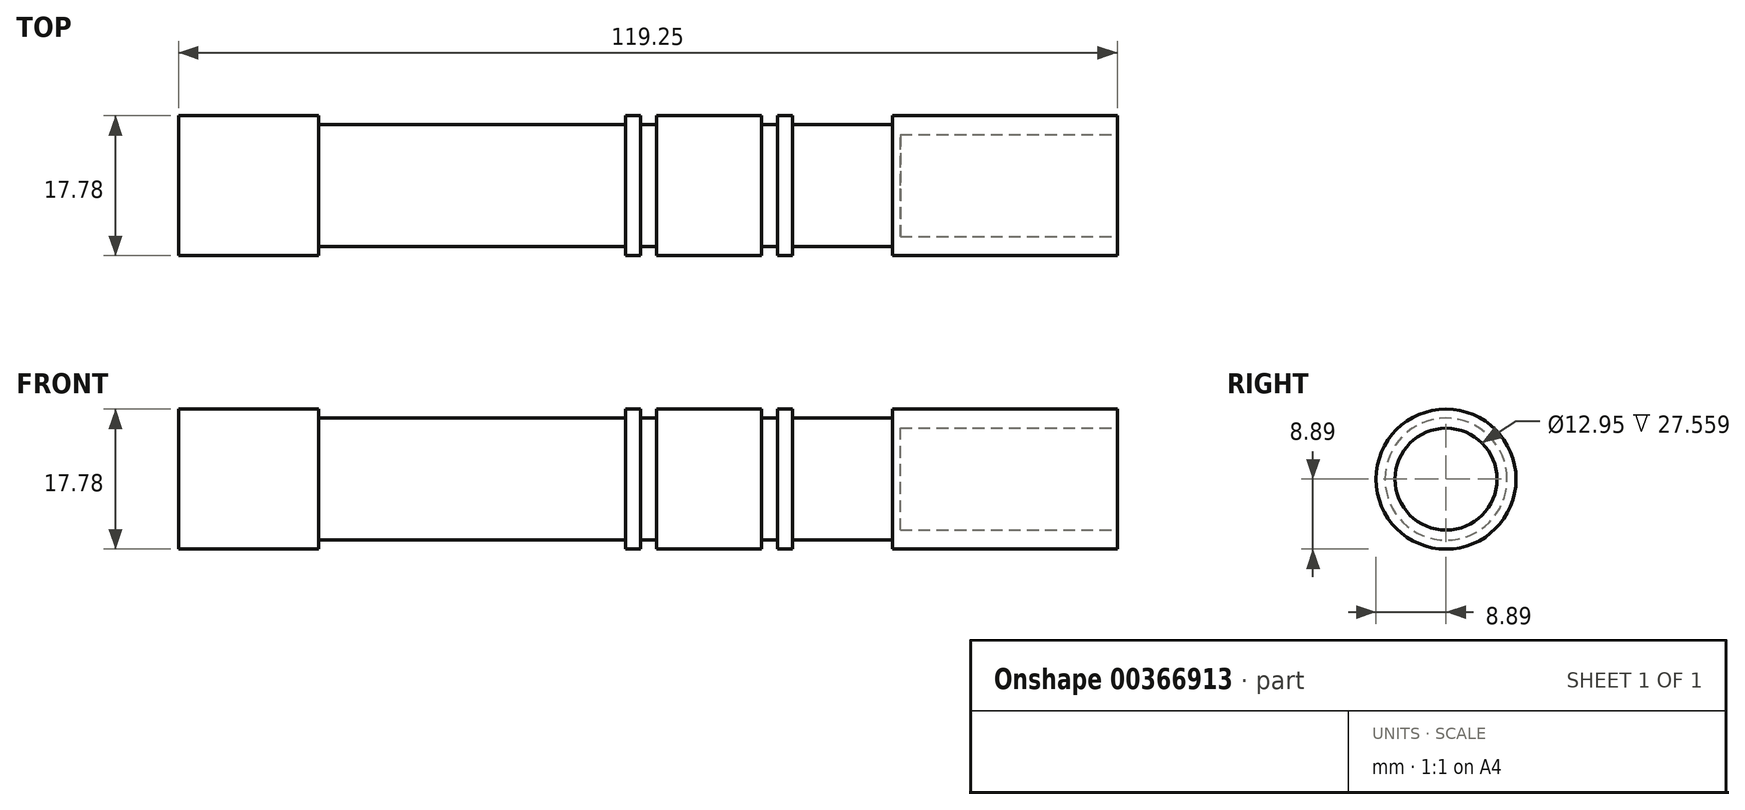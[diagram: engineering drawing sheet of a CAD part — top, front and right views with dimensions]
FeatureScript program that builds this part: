
annotation { "Feature Type Name" : "Feature", "Feature Type Description" : "" }
export const myFeature = defineFeature(function(context is Context, id is Id, definition is map)
    precondition{}
    {
        {
            var Q0;
            Q0=qCreatedBy(makeId("Right.planeOp"),FACE);
            var sketch = newSketch(context, id + "F0", { "sketchPlane" : qUnion([Q0])});
            skCircle(sketch, "E0", {"center": v(0, 0) * mm, "radius": 8.89 * mm});
            skSolve(sketch);
        }
        {
            var Q0;
            Q0 = qSketchRegion(id + "F0", true);
            extrude(context, id + "F1", {"entities" : qUnion([Q0]), "depth" : 17.78 * mm, "offsetDistance" : 25.4 * mm});
        }
        {
            var Q0;
            Q0=makeQuery(id+"F1.opExtrude","CAP_FACE",FACE,{"disambiguationData":[OSD([sQuery(id+"F0.wireOp",EDGE,"E0")])],"isStart":false});
            var sketch = newSketch(context, id + "F2", { "sketchPlane" : qUnion([Q0])});
            skCircle(sketch, "E1", {"center": v(0, 0) * mm, "radius": 7.75 * mm});
            skSolve(sketch);
        }
        {
            var Q0;
            Q0 = qSketchRegion(id + "F2", true);
            extrude(context, id + "F3", {"entities" : qUnion([Q0]), "operationType" : NewBodyOperationType.ADD, "depth" : 39 * mm, "offsetDistance" : 25.4 * mm});
        }
        {
            var Q0;
            Q0=makeQuery(id+"F3.opExtrude","CAP_FACE",FACE,{"disambiguationData":[OSD([sQuery(id+"F2.wireOp",EDGE,"E1")])],"isStart":false});
            var sketch = newSketch(context, id + "F4", { "sketchPlane" : qUnion([Q0])});
            skCircle(sketch, "E2", {"center": v(0, 0) * mm, "radius": 8.9 * mm});
            skSolve(sketch);
        }
        {
            var Q0;
            Q0 = qSketchRegion(id + "F4", true);
            extrude(context, id + "F5", {"entities" : qUnion([Q0]), "operationType" : NewBodyOperationType.ADD, "depth" : 1.9 * mm, "offsetDistance" : 25.4 * mm});
        }
        {
            var Q0;
            Q0=makeQuery(id+"F5.opExtrude","CAP_FACE",FACE,{"disambiguationData":[OSD([sQuery(id+"F4.wireOp",EDGE,"E2")])],"isStart":false});
            var sketch = newSketch(context, id + "F6", { "sketchPlane" : qUnion([Q0])});
            skCircle(sketch, "E3", {"center": v(0, 0) * mm, "radius": 7.75 * mm});
            skSolve(sketch);
        }
        {
            var Q0;
            Q0 = qSketchRegion(id + "F6", true);
            extrude(context, id + "F7", {"entities" : qUnion([Q0]), "operationType" : NewBodyOperationType.ADD, "depth" : 2.03 * mm, "offsetDistance" : 25.4 * mm});
        }
        {
            var Q0;
            Q0=makeQuery(id+"F7.opExtrude","CAP_FACE",FACE,{"disambiguationData":[OSD([sQuery(id+"F6.wireOp",EDGE,"E3")])],"isStart":false});
            var sketch = newSketch(context, id + "F8", { "sketchPlane" : qUnion([Q0])});
            skCircle(sketch, "E4", {"center": v(0, 0) * mm, "radius": 8.9 * mm});
            skSolve(sketch);
        }
        {
            var Q0;
            Q0 = qSketchRegion(id + "F8", true);
            extrude(context, id + "F9", {"entities" : qUnion([Q0]), "operationType" : NewBodyOperationType.ADD, "depth" : 13.33 * mm, "offsetDistance" : 25.4 * mm});
        }
        {
            var Q0;
            Q0=makeQuery(id+"F9.opExtrude","CAP_FACE",FACE,{"disambiguationData":[OSD([sQuery(id+"F8.wireOp",EDGE,"E4")])],"isStart":false});
            var sketch = newSketch(context, id + "F10", { "sketchPlane" : qUnion([Q0])});
            skCircle(sketch, "E5", {"center": v(0, 0) * mm, "radius": 7.75 * mm});
            skSolve(sketch);
        }
        {
            var Q0;
            Q0 = qSketchRegion(id + "F10", true);
            extrude(context, id + "F11", {"entities" : qUnion([Q0]), "operationType" : NewBodyOperationType.ADD, "depth" : 2.03 * mm, "offsetDistance" : 25.4 * mm});
        }
        {
            var Q0;
            Q0=makeQuery(id+"F11.opExtrude","CAP_FACE",FACE,{"disambiguationData":[OSD([sQuery(id+"F10.wireOp",EDGE,"E5")])],"isStart":false});
            var sketch = newSketch(context, id + "F12", { "sketchPlane" : qUnion([Q0])});
            skCircle(sketch, "E6", {"center": v(0, 0) * mm, "radius": 8.9 * mm});
            skSolve(sketch);
        }
        {
            var Q0;
            Q0 = qSketchRegion(id + "F12", true);
            extrude(context, id + "F13", {"entities" : qUnion([Q0]), "operationType" : NewBodyOperationType.ADD, "depth" : 1.9 * mm, "offsetDistance" : 25.4 * mm});
        }
        {
            var Q0;
            Q0=makeQuery(id+"F13.opExtrude","CAP_FACE",FACE,{"disambiguationData":[OSD([sQuery(id+"F12.wireOp",EDGE,"E6")])],"isStart":false});
            var sketch = newSketch(context, id + "F14", { "sketchPlane" : qUnion([Q0])});
            skCircle(sketch, "E7", {"center": v(0, 0) * mm, "radius": 7.75 * mm});
            skSolve(sketch);
        }
        {
            var Q0;
            Q0 = qSketchRegion(id + "F14", true);
            extrude(context, id + "F15", {"entities" : qUnion([Q0]), "operationType" : NewBodyOperationType.ADD, "depth" : 12.7 * mm, "offsetDistance" : 25.4 * mm});
        }
        {
            var Q0;
            Q0=makeQuery(id+"F15.opExtrude","CAP_FACE",FACE,{"disambiguationData":[OSD([sQuery(id+"F14.wireOp",EDGE,"E7")])],"isStart":false});
            var sketch = newSketch(context, id + "F16", { "sketchPlane" : qUnion([Q0])});
            skCircle(sketch, "E8", {"center": v(0, 0) * mm, "radius": 8.9 * mm});
            skSolve(sketch);
        }
        {
            var Q0;
            Q0 = qSketchRegion(id + "F16", true);
            extrude(context, id + "F17", {"entities" : qUnion([Q0]), "operationType" : NewBodyOperationType.ADD, "depth" : 28.57 * mm, "offsetDistance" : 25.4 * mm});
        }
        {
            var Q0;
            Q0=makeQuery(id+"F17.opExtrude","CAP_FACE",FACE,{"disambiguationData":[OSD([sQuery(id+"F16.wireOp",EDGE,"E8")])],"isStart":false});
            var sketch = newSketch(context, id + "F18", { "sketchPlane" : qUnion([Q0])});
            skCircle(sketch, "E9", {"center": v(0, 0) * mm, "radius": 6.48 * mm});
            skSolve(sketch);
        }
        {
            var Q0;
            Q0 = qSketchRegion(id + "F18", true);
            extrude(context, id + "F19", {"entities" : qUnion([Q0]), "operationType" : NewBodyOperationType.REMOVE, "oppositeDirection" : true, "depth" : 27.56 * mm, "offsetDistance" : 25.4 * mm});
        }
    });
